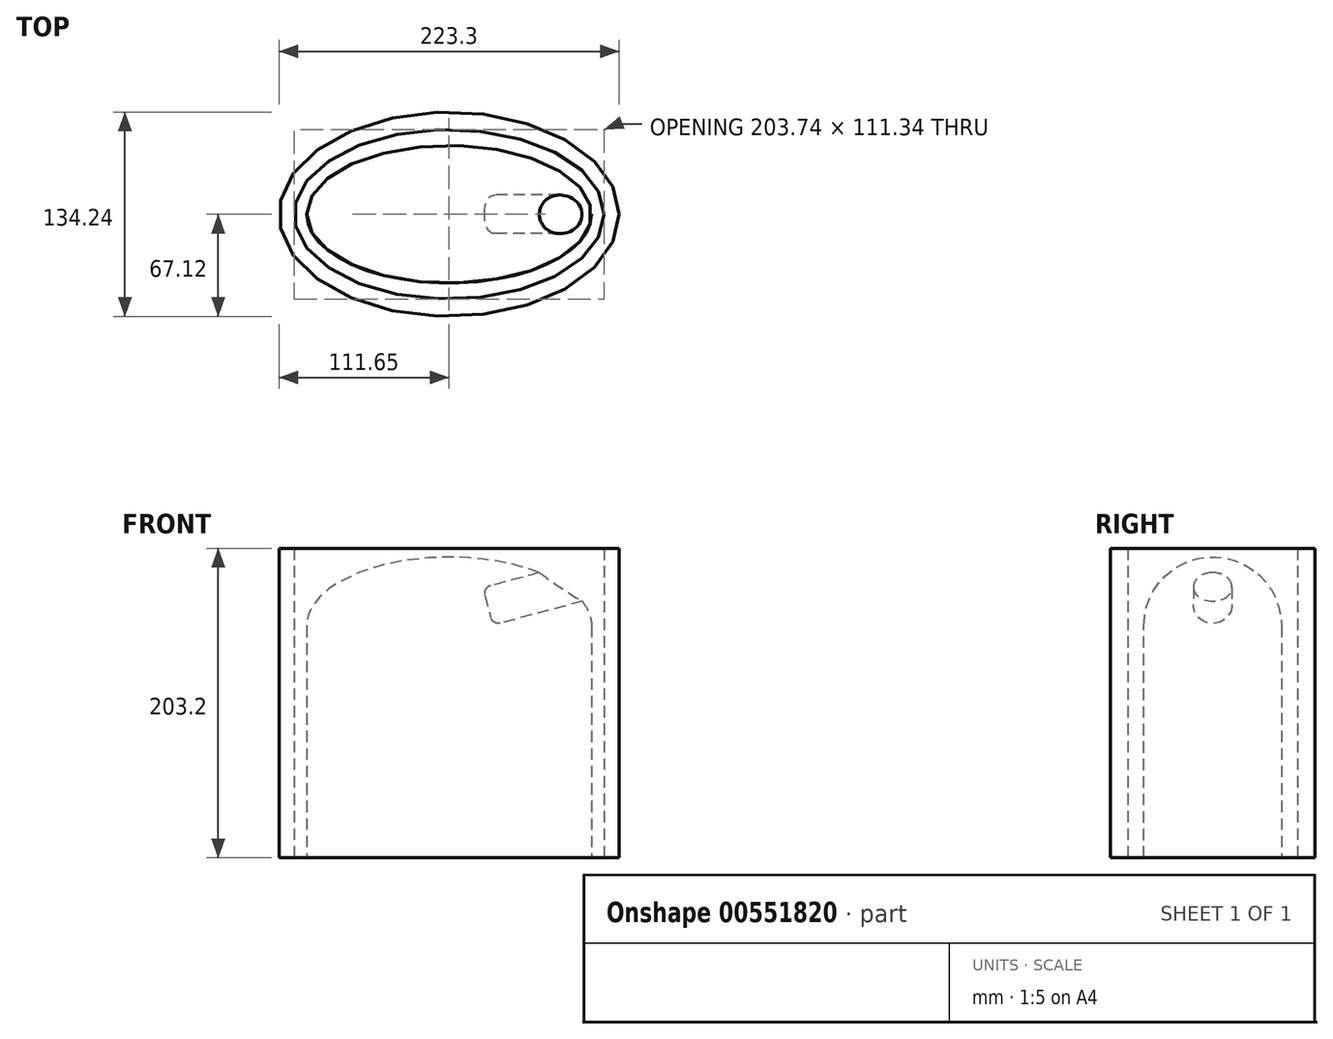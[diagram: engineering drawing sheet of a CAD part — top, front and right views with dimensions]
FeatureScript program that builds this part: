
annotation { "Feature Type Name" : "Feature", "Feature Type Description" : "" }
export const myFeature = defineFeature(function(context is Context, id is Id, definition is map)
    precondition{}
    {
        {
            var Q0;
            Q0=qCreatedBy(makeId("Top.planeOp"),FACE);
            var sketch = newSketch(context, id + "F0", { "sketchPlane" : qUnion([Q0])});
            skEllipse(sketch, "E0", {"center": v(0, 0) * mm, "majorRadius": 93.53 * mm, "minorRadius": 45.17 * mm, "majorAxis": v(-1, 0)});
            skSolve(sketch);
        }
        {
            var Q0;
            Q0 = qSketchRegion(id + "F0", true);
            extrude(context, id + "F1", {"entities" : qUnion([Q0]), "depth" : 152.4 * mm, "offsetDistance" : 25.4 * mm});
        }
        {
            var Q0;
            Q0=qCreatedBy(makeId("Top.planeOp"),FACE);
            var sketch = newSketch(context, id + "F2", { "sketchPlane" : qUnion([Q0])});
            skEllipse(sketch, "E1", {"center": v(0, 0) * mm, "majorRadius": 101.87 * mm, "minorRadius": 55.67 * mm, "majorAxis": v(1, 0)});
            skEllipse(sketch, "E2", {"center": v(0, 0) * mm, "majorRadius": 111.65 * mm, "minorRadius": 67.12 * mm, "majorAxis": v(1, 0)});
            skSolve(sketch);
        }
        {
            var Q0;
            Q0 = qSketchRegion(id + "F2", true);
            extrude(context, id + "F3", {"entities" : qUnion([Q0]), "depth" : 203.2 * mm, "offsetDistance" : 25.4 * mm});
        }
        {
            var Q0;
            Q0=makeQuery(id+"F1.opExtrude","CAP_FACE",FACE,{"disambiguationData":[OSD([sQuery(id+"F0.wireOp",EDGE,"E0")])],"isStart":false});
            var sketch = newSketch(context, id + "F4", { "sketchPlane" : qUnion([Q0])});
            skLineSegment(sketch, "E3", {"start": v(-93.53, 0) * mm, "end": v(93.53, 0) * mm});
            skSolve(sketch);
        }
        {
            var Q0;
            {var subQ0=sQuery(id+"F4.wireOp",EDGE,"E3");Q0=makeQuery(id+"F4.imprint","IMPRINT",FACE,{"disambiguationData":[TD([[makeQuery(id+"F4.imprint","IMPRINT",EDGE,{"derivedFrom":subQ0}),1.0]])]});}
            var Q1;
            Q1=sQuery(id+"F4.wireOp",EDGE,"E3");
            revolve(context, id + "F5", {"operationType" : NewBodyOperationType.ADD, "entities" : qUnion([Q0]), "axis" : qUnion([Q1]), "revolveType" : RevolveType.ONE_DIRECTION, "angle" : 180 * degree});
        }
        {
            var Q0;
            Q0=qCreatedBy(makeId("Right.planeOp"),FACE);
            cPlane(context, id + "F6", {"entities" : qUnion([Q0]), "cplaneType" : CPlaneType.OFFSET, "offset" : 25.4 * mm, "width" : 152.4 * mm, "height" : 152.4 * mm});
        }
        {
            var Q0;
            Q0=qCreatedBy(id+"F6.planeOp",FACE);
            var sketch = newSketch(context, id + "F7", { "sketchPlane" : qUnion([Q0])});
            skLineSegment(sketch, "E4", {"start": v(58.67, 165.1) * mm, "end": v(-72.77, 165.1) * mm, "construction": true});
            skSolve(sketch);
        }
        {
            var Q0;
            Q0=sQuery(id+"F7.wireOp",EDGE,"E4");
            var Q1;
            Q1=qCreatedBy(id+"F6.planeOp",FACE);
            cPlane(context, id + "F8", {"entities" : qUnion([Q0, Q1]), "cplaneType" : CPlaneType.LINE_ANGLE, "offset" : 25.4 * mm, "angle" : 15 * degree, "width" : 152.4 * mm, "height" : 152.4 * mm});
        }
        {
            var Q0;
            Q0=qCreatedBy(id+"F8.planeOp",FACE);
            var sketch = newSketch(context, id + "F9", { "sketchPlane" : qUnion([Q0])});
            skCircle(sketch, "E5", {"center": v(0, 152.9) * mm, "radius": 12.7 * mm});
            skSolve(sketch);
        }
        {
            var Q0;
            Q0 = qSketchRegion(id + "F9", true);
            var Q1;
            Q1=sQuery(id+"F9.wireOp",EDGE,"E5");
            var Q2;
            Q2=makeQuery(id+"F5.opRevolve","SWEPT_FACE",FACE,{"disambiguationData":[OSD([sQuery(id+"F0.wireOp",EDGE,"E0")])]});
            extrude(context, id + "F10", {"entities" : qUnion([Q0]), "operationType" : NewBodyOperationType.REMOVE, "surfaceEntities" : qUnion([Q1]), "endBound" : BoundingType.UP_TO_SURFACE, "oppositeDirection" : true, "depth" : 25.4 * mm, "endBoundEntityFace" : qUnion([Q2]), "offsetDistance" : 25.4 * mm});
        }
        {
            var Q0;
            Q0=makeQuery(id+"F10.boolean.opBoolean","COPY",EDGE,{"derivedFrom":makeQuery(id+"F10.opExtrude","CAP_EDGE",EDGE,{"disambiguationData":[OSD([sQuery(id+"F9.wireOp",EDGE,"E5")])],"isStart":true})});
            fillet(context, id + "F11", {"entities" : qUnion([Q0]), "radius" : 5.08 * mm, "tangentPropagation" : true, "allowEdgeOverflow" : false});
        }
        {
            var Q0;
            Q0=qCreatedBy(makeId("Right.planeOp"),FACE);
            cPlane(context, id + "F12", {"entities" : qUnion([Q0]), "cplaneType" : CPlaneType.OFFSET, "offset" : 101.6 * mm, "width" : 152.4 * mm, "height" : 152.4 * mm});
        }
    });
